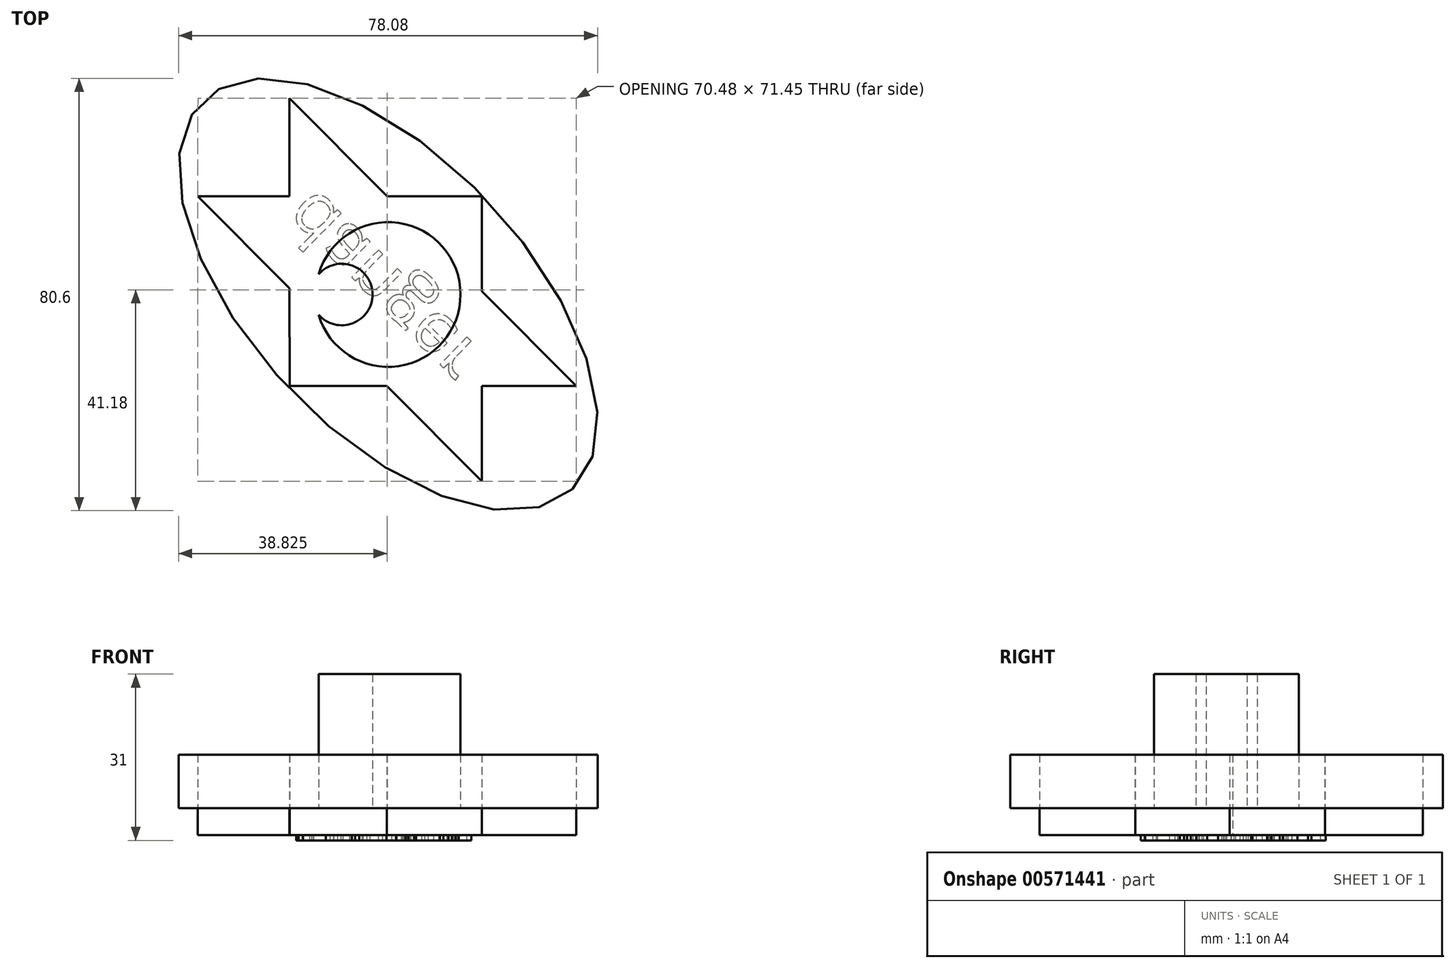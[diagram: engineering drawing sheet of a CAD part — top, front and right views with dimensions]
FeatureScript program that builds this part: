
annotation { "Feature Type Name" : "Feature", "Feature Type Description" : "" }
export const myFeature = defineFeature(function(context is Context, id is Id, definition is map)
    precondition{}
    {
        {
            var Q0;
            Q0=qCreatedBy(makeId("Top.planeOp"),FACE);
            var sketch = newSketch(context, id + "F0", { "sketchPlane" : qUnion([Q0])});
            skLineSegment(sketch, "E0", {"start": v(-35.46, 18.3) * mm, "end": v(17.46, -34.84) * mm});
            skLineSegment(sketch, "E1", {"start": v(17.46, -34.84) * mm, "end": v(17.46, 18.32) * mm});
            skLineSegment(sketch, "E2", {"start": v(17.46, 18.32) * mm, "end": v(-35.46, 18.3) * mm});
            skLineSegment(sketch, "E3", {"start": v(-18.38, -17.07) * mm, "end": v(-18.4, 36.6) * mm});
            skLineSegment(sketch, "E4", {"start": v(-18.4, 36.6) * mm, "end": v(35.03, -17.04) * mm});
            skLineSegment(sketch, "E5", {"start": v(35.03, -17.04) * mm, "end": v(-18.38, -17.07) * mm});
            skSolve(sketch);
        }
        {
            var Q0;
            {var subQ0=sQuery(id+"F0.wireOp",EDGE,"E3");var subQ1=sQuery(id+"F0.wireOp",EDGE,"E0");var subQ2=makeQuery(id+"F0.imprint","INTERSECT",VERTEX,{"derivedFrom":[subQ1,subQ0]});Q0=makeQuery(id+"F0.imprint","IMPRINT",FACE,{"disambiguationData":[TD([[makeQuery(id+"F0.imprint","IMPRINT",EDGE,{"disambiguationData":[TD([[subQ2,-1.0]])],"derivedFrom":subQ1}),1.0]])]});}
            var Q1;
            {var subQ0=sQuery(id+"F0.wireOp",EDGE,"E3");var subQ1=sQuery(id+"F0.wireOp",EDGE,"E0");var subQ2=makeQuery(id+"F0.imprint","INTERSECT",VERTEX,{"derivedFrom":[subQ1,subQ0]});Q1=makeQuery(id+"F0.imprint","IMPRINT",FACE,{"disambiguationData":[TD([[makeQuery(id+"F0.imprint","IMPRINT",EDGE,{"disambiguationData":[TD([[subQ2,-1.0]])],"derivedFrom":subQ1}),-1.0]])]});}
            var Q2;
            {var subQ0=sQuery(id+"F0.wireOp",EDGE,"E1");var subQ1=sQuery(id+"F0.wireOp",EDGE,"E0");var subQ2=makeQuery(id+"F0.imprint","INTERSECT",VERTEX,{"derivedFrom":[subQ1,subQ0]});Q2=makeQuery(id+"F0.imprint","IMPRINT",FACE,{"disambiguationData":[TD([[makeQuery(id+"F0.imprint","IMPRINT",EDGE,{"disambiguationData":[TD([[subQ2,1.0]])],"derivedFrom":subQ1}),1.0]])]});}
            var Q3;
            {var subQ0=sQuery(id+"F0.wireOp",EDGE,"E5");var subQ1=sQuery(id+"F0.wireOp",EDGE,"E1");var subQ2=makeQuery(id+"F0.imprint","INTERSECT",VERTEX,{"derivedFrom":[subQ1,subQ0]});Q3=makeQuery(id+"F0.imprint","IMPRINT",FACE,{"disambiguationData":[TD([[makeQuery(id+"F0.imprint","IMPRINT",EDGE,{"disambiguationData":[TD([[subQ2,-1.0]])],"derivedFrom":subQ1}),-1.0]])]});}
            var Q4;
            {var subQ0=sQuery(id+"F0.wireOp",EDGE,"E2");var subQ1=sQuery(id+"F0.wireOp",EDGE,"E0");var subQ2=makeQuery(id+"F0.imprint","INTERSECT",VERTEX,{"derivedFrom":[subQ1,subQ0]});Q4=makeQuery(id+"F0.imprint","IMPRINT",FACE,{"disambiguationData":[TD([[makeQuery(id+"F0.imprint","IMPRINT",EDGE,{"disambiguationData":[TD([[subQ2,-1.0]])],"derivedFrom":subQ1}),1.0]])]});}
            var Q5;
            {var subQ0=sQuery(id+"F0.wireOp",EDGE,"E2");var subQ1=sQuery(id+"F0.wireOp",EDGE,"E1");var subQ2=makeQuery(id+"F0.imprint","INTERSECT",VERTEX,{"derivedFrom":[subQ1,subQ0]});Q5=makeQuery(id+"F0.imprint","IMPRINT",FACE,{"disambiguationData":[TD([[makeQuery(id+"F0.imprint","IMPRINT",EDGE,{"disambiguationData":[TD([[subQ2,1.0]])],"derivedFrom":subQ1}),1.0]])]});}
            var Q6;
            {var subQ0=sQuery(id+"F0.wireOp",EDGE,"E4");var subQ1=sQuery(id+"F0.wireOp",EDGE,"E2");var subQ2=makeQuery(id+"F0.imprint","INTERSECT",VERTEX,{"derivedFrom":[subQ1,subQ0]});Q6=makeQuery(id+"F0.imprint","IMPRINT",FACE,{"disambiguationData":[TD([[makeQuery(id+"F0.imprint","IMPRINT",EDGE,{"disambiguationData":[TD([[subQ2,-1.0]])],"derivedFrom":subQ1}),-1.0]])]});}
            extrude(context, id + "F1", {"entities" : qUnion([Q0, Q1, Q2, Q3, Q4, Q5, Q6]), "depth" : 5 * mm, "offsetDistance" : 25.4 * mm});
        }
        {
            var Q0;
            Q0=makeQuery(id+"F1.opExtrude","CAP_FACE",FACE,{"disambiguationData":[OSD([sQuery(id+"F0.wireOp",EDGE,"E0"),sQuery(id+"F0.wireOp",EDGE,"E1"),sQuery(id+"F0.wireOp",EDGE,"E2"),sQuery(id+"F0.wireOp",EDGE,"E3"),sQuery(id+"F0.wireOp",EDGE,"E4"),sQuery(id+"F0.wireOp",EDGE,"E5")])],"isStart":false});
            var sketch = newSketch(context, id + "F2", { "sketchPlane" : qUnion([Q0])});
            skEllipse(sketch, "E6", {"center": v(0, 0) * mm, "majorRadius": 50 * mm, "minorRadius": 25.45 * mm, "majorAxis": v(0.69, -0.73)});
            skSolve(sketch);
        }
        {
            var Q0;
            Q0=makeQuery(id+"F2.imprint","IMPRINT",FACE,{"disambiguationData":[TD([[makeQuery(id+"F2.imprint","IMPRINT",EDGE,{"derivedFrom":sQuery(id+"F2.wireOp",EDGE,"E6")}),1.0]])]});
            extrude(context, id + "F3", {"entities" : qUnion([Q0]), "depth" : 10 * mm, "offsetDistance" : 25.4 * mm});
        }
        {
            var Q0;
            Q0=makeQuery(id+"F1.opExtrude","CAP_FACE",FACE,{"disambiguationData":[OSD([sQuery(id+"F0.wireOp",EDGE,"E0"),sQuery(id+"F0.wireOp",EDGE,"E1"),sQuery(id+"F0.wireOp",EDGE,"E2"),sQuery(id+"F0.wireOp",EDGE,"E3"),sQuery(id+"F0.wireOp",EDGE,"E4"),sQuery(id+"F0.wireOp",EDGE,"E5")])],"isStart":true});
            var sketch = newSketch(context, id + "F4", { "sketchPlane" : qUnion([Q0])});
            skLineSegment(sketch, "E7", {"start": v(20.77, 20.31) * mm, "end": v(-18.39, -18.3) * mm, "construction": true});
            skText(sketch, "E8", { "text": "danger", "fontName": "OpenSans-Regular.ttf"});
            const initialGuessF4  = {"E8": [-0.01377, -0.02014, 0.71204, 0.70214, 0.00967]};
            skSetInitialGuess(sketch, initialGuessF4);
            skSolve(sketch);
        }
        {
            var Q0;
            Q0 = qSketchRegion(id + "F4", true);
            extrude(context, id + "F5", {"entities" : qUnion([Q0]), "operationType" : NewBodyOperationType.ADD, "depth" : 1 * mm, "offsetDistance" : 25 * mm});
        }
        {
            var Q0;
            Q0=makeQuery(id+"F1.opExtrude","CAP_FACE",FACE,{"disambiguationData":[OSD([sQuery(id+"F0.wireOp",EDGE,"E0"),sQuery(id+"F0.wireOp",EDGE,"E1"),sQuery(id+"F0.wireOp",EDGE,"E2"),sQuery(id+"F0.wireOp",EDGE,"E3"),sQuery(id+"F0.wireOp",EDGE,"E4"),sQuery(id+"F0.wireOp",EDGE,"E5")])],"isStart":false});
            var sketch = newSketch(context, id + "F6", { "sketchPlane" : qUnion([Q0])});
            skCircle(sketch, "E9", {"center": v(-8.65, 0) * mm, "radius": 5.74 * mm});
            skCircle(sketch, "E10", {"center": v(0, 0) * mm, "radius": 13.5 * mm});
            skSolve(sketch);
        }
        {
            var Q0;
            {var subQ0=sQuery(id+"F6.wireOp",EDGE,"E10");var subQ1=sQuery(id+"F6.wireOp",EDGE,"E9");var subQ2=makeQuery(id+"F6.imprint","INTERSECT",VERTEX,{"disambiguationData":[OD(0.0)],"derivedFrom":[subQ1,subQ0]});Q0=makeQuery(id+"F6.imprint","IMPRINT",FACE,{"disambiguationData":[TD([[makeQuery(id+"F6.imprint","IMPRINT",EDGE,{"disambiguationData":[TD([[subQ2,-1.0]])],"derivedFrom":subQ1}),-1.0]])]});}
            extrude(context, id + "F7", {"entities" : qUnion([Q0]), "operationType" : NewBodyOperationType.ADD, "depth" : 25 * mm, "offsetDistance" : 25 * mm});
        }
    });
